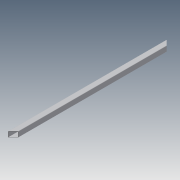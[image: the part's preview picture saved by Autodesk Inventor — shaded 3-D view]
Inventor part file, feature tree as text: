
AUTODESK INVENTOR PART (.ipt)
format: ipt  version: 2014 (Build 180170000, 170)  size: 107,008 bytes
history: native  units: in
note: dims shown in document units (in); Inventor stores cm internally (conversion verified against a paired STEP export)
features: extrude x2, sketch x2
ambient origin geometry x8: Origin, YZ Plane, XZ Plane, XY Plane, X Axis, Y Axis, Z Axis, Center Point
bodies: Solid1 (feature_tree)
feature tree (4):
  extrude  "Extrusion1"  Depth=1.0in
  extrude  "Extrusion2"  Depth=0.063in
  sketch  "Sketch1"  dims[d0=1.0in d1=1.0in]
  sketch  "Sketch2"  dims[d2=0.07in d3=0.063in d4=29.5in d5=0.0in d7=45.0deg d9=45.0deg d10=1.0in d11=0.0in]
